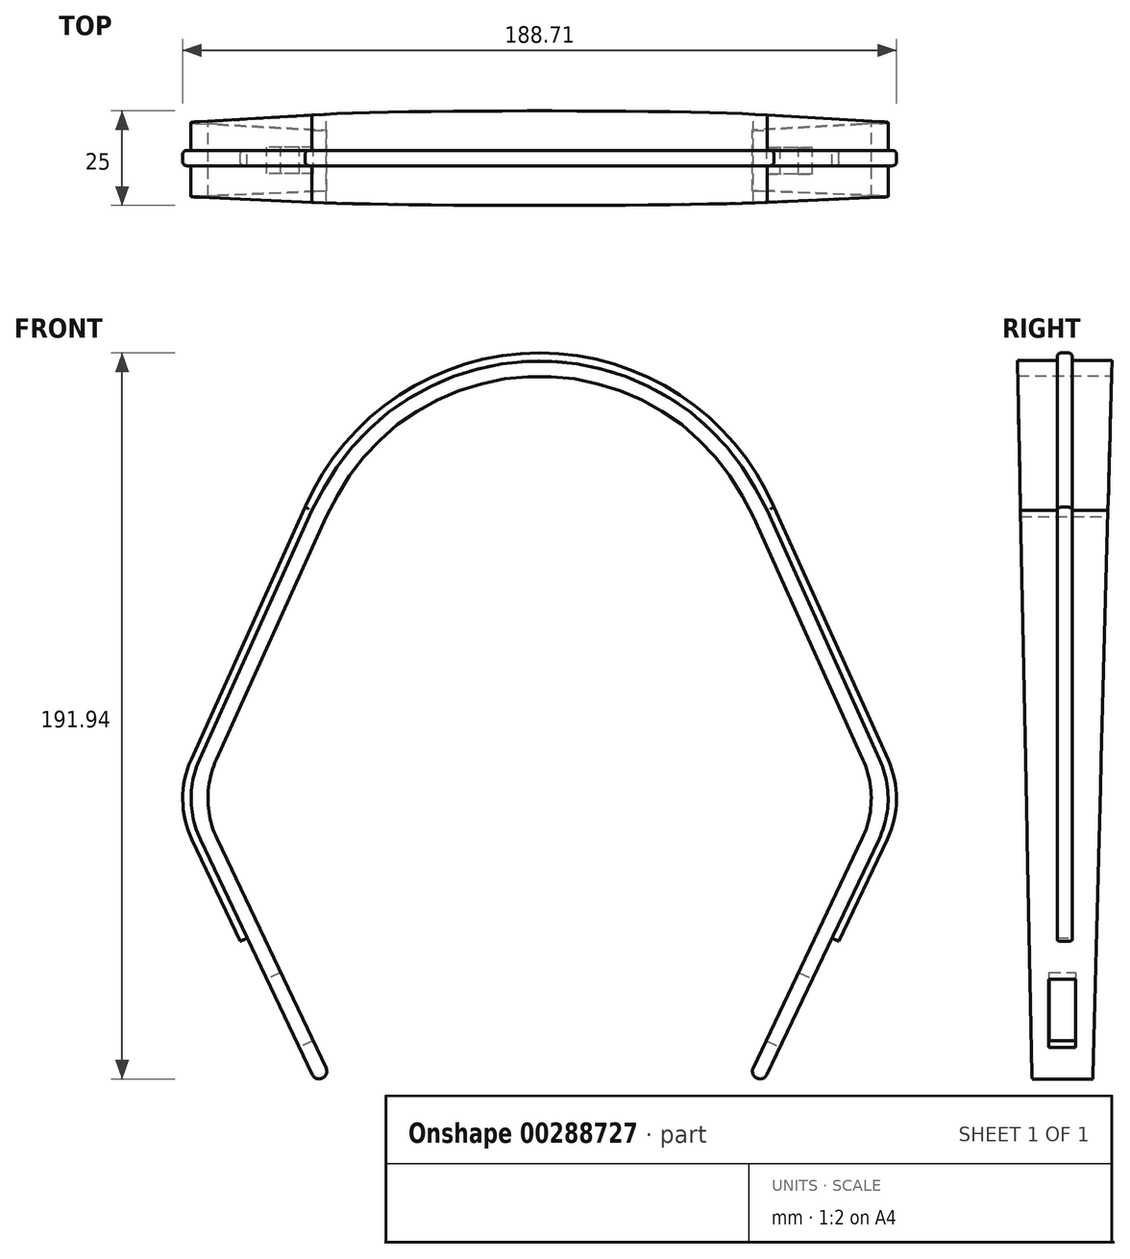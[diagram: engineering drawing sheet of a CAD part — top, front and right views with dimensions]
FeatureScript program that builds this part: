
annotation { "Feature Type Name" : "Feature", "Feature Type Description" : "" }
export const myFeature = defineFeature(function(context is Context, id is Id, definition is map)
    precondition{}
    {
        {
            var Q0;
            Q0=qCreatedBy(makeId("Right.planeOp"),FACE);
            cPlane(context, id + "F0", {"entities" : qUnion([Q0]), "cplaneType" : CPlaneType.OFFSET, "offset" : 144.2 * mm, "oppositeDirection" : true, "width" : 150 * mm, "height" : 150 * mm});
        }
        {
            var Q0;
            Q0=qCreatedBy(makeId("Front.planeOp"),FACE);
            var sketch = newSketch(context, id + "F1", { "sketchPlane" : qUnion([Q0])});
            skLineSegment(sketch, "E0", {"start": v(94.64, 16.15) * mm, "end": v(60.84, -54.85) * mm});
            skPoint(sketch, "E1.orphan", {"position": v(-52.06, -54.85) * mm});
            skLineSegment(sketch, "E2", {"start": v(94.64, 16.15) * mm, "end": v(60.84, 90.95) * mm});
            skLineSegment(sketch, "E3.MirrorCS", {"start": v(-85.86, 16.15) * mm, "end": v(-52.06, -54.85) * mm});
            skLineSegment(sketch, "E4.MirrorCS", {"start": v(-85.86, 16.15) * mm, "end": v(-52.06, 90.95) * mm});
            skArc(sketch, "E5", {"start": v(60.84, 90.95) * mm, "mid": v(4.39, 128.15) * mm, "end": v(-52.06, 90.95) * mm});
            skLineSegment(sketch, "E6.0", {"start": v(-90.32, 16.1) * mm, "end": v(-55.71, -56.59) * mm});
            skLineSegment(sketch, "E6.1", {"start": v(99.1, 16.1) * mm, "end": v(64.49, -56.59) * mm});
            skLineSegment(sketch, "E6.2", {"start": v(99.1, 16.1) * mm, "end": v(64.54, 92.58) * mm});
            skArc(sketch, "E6.3", {"start": v(64.54, 92.58) * mm, "mid": v(4.39, 132.2) * mm, "end": v(-55.76, 92.58) * mm});
            skLineSegment(sketch, "E6.4", {"start": v(-90.32, 16.1) * mm, "end": v(-55.76, 92.58) * mm});
            skArc(sketch, "E7", {"start": v(-55.71, -56.59) * mm, "mid": v(-53.02, -57.54) * mm, "end": v(-52.06, -54.85) * mm});
            skArc(sketch, "E8", {"start": v(60.84, -54.85) * mm, "mid": v(61.8, -57.54) * mm, "end": v(64.49, -56.59) * mm});
            skSolve(sketch);
        }
        {
            var Q0;
            Q0 = qSketchRegion(id + "F1", true);
            extrude(context, id + "F2", {"entities" : qUnion([Q0]), "depth" : 10.5 * mm});
        }
        {
            var Q0;
            Q0=makeQuery(id+"F2.opExtrude","CAP_FACE",FACE,{"disambiguationData":[OSD([sQuery(id+"F1.wireOp",EDGE,"E0"),sQuery(id+"F1.wireOp",EDGE,"E2"),sQuery(id+"F1.wireOp",EDGE,"E3.MirrorCS"),sQuery(id+"F1.wireOp",EDGE,"E4.MirrorCS"),sQuery(id+"F1.wireOp",EDGE,"E5"),sQuery(id+"F1.wireOp",EDGE,"E6.0"),sQuery(id+"F1.wireOp",EDGE,"E6.1"),sQuery(id+"F1.wireOp",EDGE,"E6.2"),sQuery(id+"F1.wireOp",EDGE,"E6.3"),sQuery(id+"F1.wireOp",EDGE,"E6.4"),sQuery(id+"F1.wireOp",EDGE,"E7"),sQuery(id+"F1.wireOp",EDGE,"E8")])],"isStart":false});
            var sketch = newSketch(context, id + "F3", { "sketchPlane" : qUnion([Q0])});
            skLineSegment(sketch, "E9.0.0", {"start": v(-72.9, -20.47) * mm, "end": v(-55.71, -56.59) * mm});
            skArc(sketch, "E9.0.1", {"start": v(-55.71, -56.59) * mm, "mid": v(-53.02, -57.54) * mm, "end": v(-52.06, -54.85) * mm});
            skLineSegment(sketch, "E9.0.2", {"start": v(-52.06, -54.85) * mm, "end": v(-85.86, 16.15) * mm});
            skLineSegment(sketch, "E9.0.3", {"start": v(-85.86, 16.15) * mm, "end": v(-52.06, 90.95) * mm});
            skArc(sketch, "E9.0.4", {"start": v(-52.06, 90.95) * mm, "mid": v(4.39, 128.15) * mm, "end": v(60.84, 90.95) * mm});
            skLineSegment(sketch, "E9.0.5", {"start": v(60.84, 90.95) * mm, "end": v(94.64, 16.15) * mm});
            skLineSegment(sketch, "E9.0.6", {"start": v(94.64, 16.15) * mm, "end": v(60.84, -54.85) * mm});
            skArc(sketch, "E9.0.7", {"start": v(60.84, -54.85) * mm, "mid": v(61.8, -57.54) * mm, "end": v(64.49, -56.59) * mm});
            skLineSegment(sketch, "E9.0.8", {"start": v(64.49, -56.59) * mm, "end": v(81.68, -20.47) * mm});
            skLineSegment(sketch, "E10", {"start": v(-72.9, -20.47) * mm, "end": v(-74.71, -21.33) * mm});
            skLineSegment(sketch, "E11", {"start": v(-74.71, -21.33) * mm, "end": v(-92.53, 16.09) * mm});
            skLineSegment(sketch, "E12.0", {"start": v(-57.59, 93.4) * mm, "end": v(-92.14, 16.93) * mm});
            skLineSegment(sketch, "E13", {"start": v(-92.14, 16.93) * mm, "end": v(-92.53, 16.09) * mm});
            skPoint(sketch, "E9.0.11.end.orphan", {"position": v(-90.32, 16.1) * mm});
            skLineSegment(sketch, "E14.MirrorCS", {"start": v(66.36, 93.4) * mm, "end": v(100.92, 16.93) * mm});
            skLineSegment(sketch, "E15.MirrorCS", {"start": v(83.49, -21.33) * mm, "end": v(101.3, 16.09) * mm});
            skLineSegment(sketch, "E16.MirrorCS", {"start": v(100.92, 16.93) * mm, "end": v(101.3, 16.09) * mm});
            skArc(sketch, "E17", {"start": v(66.36, 93.4) * mm, "mid": v(4.39, 134.2) * mm, "end": v(-57.59, 93.4) * mm});
            skLineSegment(sketch, "E18", {"start": v(83.49, -21.33) * mm, "end": v(81.68, -20.47) * mm});
            skPoint(sketch, "E19.orphan", {"position": v(99.1, 16.1) * mm});
            skSolve(sketch);
        }
        {
            var Q0;
            Q0 = qSketchRegion(id + "F3", true);
            extrude(context, id + "F4", {"entities" : qUnion([Q0]), "operationType" : NewBodyOperationType.ADD, "depth" : 4 * mm});
        }
        {
            var Q0;
            Q0=makeQuery(id+"F4.opExtrude","CAP_FACE",FACE,{"disambiguationData":[OSD([sQuery(id+"F3.wireOp",EDGE,"E9.0.0"),sQuery(id+"F3.wireOp",EDGE,"E9.0.1"),sQuery(id+"F3.wireOp",EDGE,"E9.0.2"),sQuery(id+"F3.wireOp",EDGE,"E9.0.3"),sQuery(id+"F3.wireOp",EDGE,"E9.0.4"),sQuery(id+"F3.wireOp",EDGE,"E9.0.5"),sQuery(id+"F3.wireOp",EDGE,"E9.0.6"),sQuery(id+"F3.wireOp",EDGE,"E9.0.7"),sQuery(id+"F3.wireOp",EDGE,"E9.0.8"),sQuery(id+"F3.wireOp",EDGE,"E10"),sQuery(id+"F3.wireOp",EDGE,"E11"),sQuery(id+"F3.wireOp",EDGE,"E12.0"),sQuery(id+"F3.wireOp",EDGE,"E13"),sQuery(id+"F3.wireOp",EDGE,"E14.MirrorCS"),sQuery(id+"F3.wireOp",EDGE,"E15.MirrorCS"),sQuery(id+"F3.wireOp",EDGE,"E16.MirrorCS"),sQuery(id+"F3.wireOp",EDGE,"E17"),sQuery(id+"F3.wireOp",EDGE,"E18")])],"isStart":false});
            var sketch = newSketch(context, id + "F5", { "sketchPlane" : qUnion([Q0])});
            skLineSegment(sketch, "E20.0.0", {"start": v(-55.71, -56.59) * mm, "end": v(-90.32, 16.1) * mm});
            skLineSegment(sketch, "E20.0.1", {"start": v(-90.32, 16.1) * mm, "end": v(-55.76, 92.58) * mm});
            skArc(sketch, "E20.0.2", {"start": v(-55.76, 92.58) * mm, "mid": v(4.39, 132.2) * mm, "end": v(64.54, 92.58) * mm});
            skLineSegment(sketch, "E20.0.3", {"start": v(64.54, 92.58) * mm, "end": v(99.1, 16.1) * mm});
            skLineSegment(sketch, "E20.0.4", {"start": v(99.1, 16.1) * mm, "end": v(64.49, -56.59) * mm});
            skArc(sketch, "E20.0.5", {"start": v(64.49, -56.59) * mm, "mid": v(61.8, -57.54) * mm, "end": v(60.84, -54.85) * mm});
            skLineSegment(sketch, "E20.0.6", {"start": v(60.84, -54.85) * mm, "end": v(94.64, 16.15) * mm});
            skLineSegment(sketch, "E20.0.7", {"start": v(94.64, 16.15) * mm, "end": v(60.84, 90.95) * mm});
            skArc(sketch, "E20.0.8", {"start": v(60.84, 90.95) * mm, "mid": v(4.39, 128.15) * mm, "end": v(-52.06, 90.95) * mm});
            skLineSegment(sketch, "E20.0.9", {"start": v(-52.06, 90.95) * mm, "end": v(-85.86, 16.15) * mm});
            skLineSegment(sketch, "E20.0.10", {"start": v(-85.86, 16.15) * mm, "end": v(-52.06, -54.85) * mm});
            skArc(sketch, "E20.0.11", {"start": v(-52.06, -54.85) * mm, "mid": v(-53.02, -57.54) * mm, "end": v(-55.71, -56.59) * mm});
            skSolve(sketch);
        }
        {
            var Q0;
            Q0 = qSketchRegion(id + "F5", true);
            extrude(context, id + "F6", {"entities" : qUnion([Q0]), "operationType" : NewBodyOperationType.ADD, "depth" : 10.5 * mm});
        }
        {
            var Q0;
            Q0=qCreatedBy(id+"F0.planeOp",FACE);
            var sketch = newSketch(context, id + "F7", { "sketchPlane" : qUnion([Q0])});
            skLineSegment(sketch, "E21.0", {"start": v(0, 16.1) * mm, "end": v(0, 92.58) * mm});
            skLineSegment(sketch, "E22.0", {"start": v(-25, 16.1) * mm, "end": v(-25, 92.58) * mm});
            skLineSegment(sketch, "E23.0", {"start": v(-25, -56.59) * mm, "end": v(-25, 16.1) * mm});
            skLineSegment(sketch, "E24.0", {"start": v(0, 16.1) * mm, "end": v(0, -56.59) * mm});
            skLineSegment(sketch, "E25.0", {"start": v(-25, -57.74) * mm, "end": v(-25, -54.85) * mm});
            skLineSegment(sketch, "E26", {"start": v(0, -57.74) * mm, "end": v(-5.12, -57.74) * mm});
            skLineSegment(sketch, "E27.0", {"start": v(0, -57.74) * mm, "end": v(0, -54.85) * mm});
            skPoint(sketch, "E28.orphan", {"position": v(-26.23, -57.74) * mm});
            skPoint(sketch, "E29.0.end.orphan", {"position": v(0, 132.2) * mm});
            skPoint(sketch, "E30.0.end.orphan", {"position": v(-25, 132.2) * mm});
            skPoint(sketch, "E31.start.orphan", {"position": v(-13.12, -57.74) * mm});
            skLineSegment(sketch, "E32.trimOffspring", {"start": v(-21.12, -57.74) * mm, "end": v(-25, -57.74) * mm});
            skLineSegment(sketch, "E33.0", {"start": v(-25, 92.58) * mm, "end": v(-25, 132.2) * mm});
            skLineSegment(sketch, "E34.0", {"start": v(0, 92.58) * mm, "end": v(0, 132.2) * mm});
            skLineSegment(sketch, "E35", {"start": v(-21.12, -57.74) * mm, "end": v(-25, 132.2) * mm});
            skLineSegment(sketch, "E36", {"start": v(-5.12, -57.74) * mm, "end": v(0, 132.2) * mm});
            skSolve(sketch);
        }
        {
            var Q0;
            Q0 = qSketchRegion(id + "F7", true);
            extrude(context, id + "F8", {"entities" : qUnion([Q0]), "operationType" : NewBodyOperationType.REMOVE, "depth" : 274.5 * mm});
        }
        {
            var Q0;
            Q0=makeQuery(id+"F6.boolean.opBoolean","MERGE",FACE,{"derivedFrom":[makeQuery(id+"F4.boolean.opBoolean","MERGE",FACE,{"derivedFrom":[makeQuery(id+"F2.opExtrude","SWEPT_FACE",FACE,{"disambiguationData":[OSD([sQuery(id+"F1.wireOp",EDGE,"E6.0")])]}),makeQuery(id+"F4.opExtrude","SWEPT_FACE",FACE,{"disambiguationData":[OSD([sQuery(id+"F3.wireOp",EDGE,"E9.0.0")])]})]}),makeQuery(id+"F6.opExtrude","SWEPT_FACE",FACE,{"disambiguationData":[OSD([sQuery(id+"F5.wireOp",EDGE,"E20.0.0")])]})]});
            cPlane(context, id + "F9", {"entities" : qUnion([Q0]), "cplaneType" : CPlaneType.OFFSET, "offset" : 25 * mm, "width" : 150 * mm, "height" : 150 * mm});
        }
        {
            var Q0;
            Q0=qCreatedBy(id+"F9.planeOp",FACE);
            var sketch = newSketch(context, id + "F10", { "sketchPlane" : qUnion([Q0])});
            skLineSegment(sketch, "E37", {"start": v(13.12, 0.83) * mm, "end": v(16.62, 0.83) * mm});
            skLineSegment(sketch, "E38", {"start": v(16.62, 0.83) * mm, "end": v(16.62, -19.17) * mm});
            skLineSegment(sketch, "E39.MirrorCS", {"start": v(13.12, 0.83) * mm, "end": v(9.62, 0.83) * mm});
            skLineSegment(sketch, "E40.MirrorCS", {"start": v(9.62, 0.83) * mm, "end": v(9.62, -19.17) * mm});
            skLineSegment(sketch, "E41", {"start": v(9.62, -19.17) * mm, "end": v(16.62, -19.17) * mm});
            skSolve(sketch);
        }
        {
            var Q0;
            Q0 = qSketchRegion(id + "F10", true);
            extrude(context, id + "F11", {"entities" : qUnion([Q0]), "operationType" : NewBodyOperationType.REMOVE, "oppositeDirection" : true, "depth" : 42.7 * mm});
        }
        {
            var Q0;
            Q0=makeQuery(id+"F6.opExtrude","SWEPT_EDGE",EDGE,{"disambiguationData":[OSD([sQuery(id+"F5.wireOp",EDGE,"E20.0.0"),sQuery(id+"F5.wireOp",EDGE,"E20.0.1")])]});
            var Q1;
            Q1=makeQuery(id+"F4.opExtrude","SWEPT_EDGE",EDGE,{"disambiguationData":[OSD([sQuery(id+"F3.wireOp",EDGE,"E11"),sQuery(id+"F3.wireOp",EDGE,"E13")])]});
            var Q2;
            Q2=makeQuery(id+"F2.opExtrude","SWEPT_EDGE",EDGE,{"disambiguationData":[OSD([sQuery(id+"F1.wireOp",EDGE,"E6.0"),sQuery(id+"F1.wireOp",EDGE,"E6.4")])]});
            var Q3;
            Q3=makeQuery(id+"F6.boolean.opBoolean","MERGE",EDGE,{"derivedFrom":[makeQuery(id+"F4.boolean.opBoolean","MERGE",EDGE,{"derivedFrom":[makeQuery(id+"F2.opExtrude","SWEPT_EDGE",EDGE,{"disambiguationData":[OSD([sQuery(id+"F1.wireOp",EDGE,"E3.MirrorCS"),sQuery(id+"F1.wireOp",EDGE,"E4.MirrorCS")])]}),makeQuery(id+"F4.opExtrude","SWEPT_EDGE",EDGE,{"disambiguationData":[OSD([sQuery(id+"F3.wireOp",EDGE,"E9.0.2"),sQuery(id+"F3.wireOp",EDGE,"E9.0.3")])]})]}),makeQuery(id+"F6.opExtrude","SWEPT_EDGE",EDGE,{"disambiguationData":[OSD([sQuery(id+"F5.wireOp",EDGE,"E20.0.9"),sQuery(id+"F5.wireOp",EDGE,"E20.0.10")])]})]});
            fillet(context, id + "F12", {"entities" : qUnion([Q0, Q1, Q2, Q3]), "radius" : 25 * mm, "tangentPropagation" : true, "allowEdgeOverflow" : false});
        }
        {
            var Q0;
            Q0=makeQuery(id+"F6.boolean.opBoolean","MERGE",FACE,{"derivedFrom":[makeQuery(id+"F4.boolean.opBoolean","MERGE",FACE,{"derivedFrom":[makeQuery(id+"F2.opExtrude","SWEPT_FACE",FACE,{"disambiguationData":[OSD([sQuery(id+"F1.wireOp",EDGE,"E6.1")])]}),makeQuery(id+"F4.opExtrude","SWEPT_FACE",FACE,{"disambiguationData":[OSD([sQuery(id+"F3.wireOp",EDGE,"E9.0.8")])]})]}),makeQuery(id+"F6.opExtrude","SWEPT_FACE",FACE,{"disambiguationData":[OSD([sQuery(id+"F5.wireOp",EDGE,"E20.0.4")])]})]});
            cPlane(context, id + "F13", {"entities" : qUnion([Q0]), "cplaneType" : CPlaneType.OFFSET, "offset" : 25 * mm, "width" : 150 * mm, "height" : 150 * mm});
        }
        {
            var Q0;
            Q0=qCreatedBy(id+"F13.planeOp",FACE);
            var sketch = newSketch(context, id + "F14", { "sketchPlane" : qUnion([Q0])});
            skLineSegment(sketch, "E42", {"start": v(-13.19, 4.6) * mm, "end": v(-16.69, 4.6) * mm});
            skLineSegment(sketch, "E43", {"start": v(-16.69, 4.6) * mm, "end": v(-16.69, -15.4) * mm});
            skLineSegment(sketch, "E44", {"start": v(-13.19, -15.4) * mm, "end": v(-16.69, -15.4) * mm});
            skLineSegment(sketch, "E45.MirrorCS", {"start": v(-13.19, -15.4) * mm, "end": v(-9.69, -15.4) * mm});
            skLineSegment(sketch, "E46.MirrorCS", {"start": v(-9.69, 4.6) * mm, "end": v(-9.69, -15.4) * mm});
            skLineSegment(sketch, "E47.MirrorCS", {"start": v(-13.19, 4.6) * mm, "end": v(-9.69, 4.6) * mm});
            skSolve(sketch);
        }
        {
            var Q0;
            Q0 = qSketchRegion(id + "F14", true);
            extrude(context, id + "F15", {"entities" : qUnion([Q0]), "operationType" : NewBodyOperationType.REMOVE, "oppositeDirection" : true, "depth" : 50.6 * mm});
        }
        {
            var Q0;
            Q0=makeQuery(id+"F6.opExtrude","SWEPT_EDGE",EDGE,{"disambiguationData":[OSD([sQuery(id+"F5.wireOp",EDGE,"E20.0.3"),sQuery(id+"F5.wireOp",EDGE,"E20.0.4")])]});
            var Q1;
            Q1=makeQuery(id+"F2.opExtrude","SWEPT_EDGE",EDGE,{"disambiguationData":[OSD([sQuery(id+"F1.wireOp",EDGE,"E6.1"),sQuery(id+"F1.wireOp",EDGE,"E6.2")])]});
            var Q2;
            Q2=makeQuery(id+"F4.opExtrude","SWEPT_EDGE",EDGE,{"disambiguationData":[OSD([sQuery(id+"F3.wireOp",EDGE,"E15.MirrorCS"),sQuery(id+"F3.wireOp",EDGE,"E16.MirrorCS")])]});
            var Q3;
            Q3=makeQuery(id+"F6.boolean.opBoolean","MERGE",EDGE,{"derivedFrom":[makeQuery(id+"F4.boolean.opBoolean","MERGE",EDGE,{"derivedFrom":[makeQuery(id+"F2.opExtrude","SWEPT_EDGE",EDGE,{"disambiguationData":[OSD([sQuery(id+"F1.wireOp",EDGE,"E0"),sQuery(id+"F1.wireOp",EDGE,"E2")])]}),makeQuery(id+"F4.opExtrude","SWEPT_EDGE",EDGE,{"disambiguationData":[OSD([sQuery(id+"F3.wireOp",EDGE,"E9.0.5"),sQuery(id+"F3.wireOp",EDGE,"E9.0.6")])]})]}),makeQuery(id+"F6.opExtrude","SWEPT_EDGE",EDGE,{"disambiguationData":[OSD([sQuery(id+"F5.wireOp",EDGE,"E20.0.6"),sQuery(id+"F5.wireOp",EDGE,"E20.0.7")])]})]});
            fillet(context, id + "F16", {"entities" : qUnion([Q0, Q1, Q2, Q3]), "radius" : 25 * mm, "tangentPropagation" : true, "allowEdgeOverflow" : false});
        }
        {
            var Q0;
            Q0=makeQuery(id+"F4.opExtrude","CAP_EDGE",EDGE,{"disambiguationData":[OSD([sQuery(id+"F3.wireOp",EDGE,"E15.MirrorCS")])],"isStart":false});
            var Q1;
            Q1=makeQuery(id+"F4.opExtrude","CAP_EDGE",EDGE,{"disambiguationData":[OSD([sQuery(id+"F3.wireOp",EDGE,"E15.MirrorCS")])],"isStart":true});
            var Q2;
            {var subQ0=sQuery(id+"F3.wireOp",EDGE,"E16.MirrorCS");var subQ1=sQuery(id+"F3.wireOp",EDGE,"E15.MirrorCS");Q2=makeQuery(id+"F16.opFillet","BLEND_EDGE",EDGE,{"blendedFrom":[makeQuery(id+"F4.opExtrude","SWEPT_EDGE",EDGE,{"disambiguationData":[OSD([subQ1,subQ0])]}),makeQuery(id+"F4.opExtrude","CAP_FACE",FACE,{"disambiguationData":[OSD([sQuery(id+"F3.wireOp",EDGE,"E9.0.0"),sQuery(id+"F3.wireOp",EDGE,"E9.0.1"),sQuery(id+"F3.wireOp",EDGE,"E9.0.2"),sQuery(id+"F3.wireOp",EDGE,"E9.0.3"),sQuery(id+"F3.wireOp",EDGE,"E9.0.4"),sQuery(id+"F3.wireOp",EDGE,"E9.0.5"),sQuery(id+"F3.wireOp",EDGE,"E9.0.6"),sQuery(id+"F3.wireOp",EDGE,"E9.0.7"),sQuery(id+"F3.wireOp",EDGE,"E9.0.8"),sQuery(id+"F3.wireOp",EDGE,"E10"),sQuery(id+"F3.wireOp",EDGE,"E11"),sQuery(id+"F3.wireOp",EDGE,"E12.0"),sQuery(id+"F3.wireOp",EDGE,"E13"),sQuery(id+"F3.wireOp",EDGE,"E14.MirrorCS"),subQ1,subQ0,sQuery(id+"F3.wireOp",EDGE,"E17"),sQuery(id+"F3.wireOp",EDGE,"E18")])],"isStart":false})],"blendedInto":[makeQuery(id+"F4.opExtrude","CAP_FACE",FACE,{"disambiguationData":[OSD([sQuery(id+"F3.wireOp",EDGE,"E9.0.0"),sQuery(id+"F3.wireOp",EDGE,"E9.0.1"),sQuery(id+"F3.wireOp",EDGE,"E9.0.2"),sQuery(id+"F3.wireOp",EDGE,"E9.0.3"),sQuery(id+"F3.wireOp",EDGE,"E9.0.4"),sQuery(id+"F3.wireOp",EDGE,"E9.0.5"),sQuery(id+"F3.wireOp",EDGE,"E9.0.6"),sQuery(id+"F3.wireOp",EDGE,"E9.0.7"),sQuery(id+"F3.wireOp",EDGE,"E9.0.8"),sQuery(id+"F3.wireOp",EDGE,"E10"),sQuery(id+"F3.wireOp",EDGE,"E11"),sQuery(id+"F3.wireOp",EDGE,"E12.0"),sQuery(id+"F3.wireOp",EDGE,"E13"),sQuery(id+"F3.wireOp",EDGE,"E14.MirrorCS"),subQ1,subQ0,sQuery(id+"F3.wireOp",EDGE,"E17"),sQuery(id+"F3.wireOp",EDGE,"E18")])],"isStart":false})]});}
            var Q3;
            {var subQ0=sQuery(id+"F3.wireOp",EDGE,"E16.MirrorCS");var subQ1=sQuery(id+"F3.wireOp",EDGE,"E15.MirrorCS");Q3=makeQuery(id+"F16.opFillet","BLEND_EDGE",EDGE,{"blendedFrom":[makeQuery(id+"F4.opExtrude","SWEPT_EDGE",EDGE,{"disambiguationData":[OSD([subQ1,subQ0])]}),makeQuery(id+"F4.opExtrude","CAP_FACE",FACE,{"disambiguationData":[OSD([sQuery(id+"F3.wireOp",EDGE,"E9.0.0"),sQuery(id+"F3.wireOp",EDGE,"E9.0.1"),sQuery(id+"F3.wireOp",EDGE,"E9.0.2"),sQuery(id+"F3.wireOp",EDGE,"E9.0.3"),sQuery(id+"F3.wireOp",EDGE,"E9.0.4"),sQuery(id+"F3.wireOp",EDGE,"E9.0.5"),sQuery(id+"F3.wireOp",EDGE,"E9.0.6"),sQuery(id+"F3.wireOp",EDGE,"E9.0.7"),sQuery(id+"F3.wireOp",EDGE,"E9.0.8"),sQuery(id+"F3.wireOp",EDGE,"E10"),sQuery(id+"F3.wireOp",EDGE,"E11"),sQuery(id+"F3.wireOp",EDGE,"E12.0"),sQuery(id+"F3.wireOp",EDGE,"E13"),sQuery(id+"F3.wireOp",EDGE,"E14.MirrorCS"),subQ1,subQ0,sQuery(id+"F3.wireOp",EDGE,"E17"),sQuery(id+"F3.wireOp",EDGE,"E18")])],"isStart":true})],"blendedInto":[makeQuery(id+"F4.opExtrude","CAP_FACE",FACE,{"disambiguationData":[OSD([sQuery(id+"F3.wireOp",EDGE,"E9.0.0"),sQuery(id+"F3.wireOp",EDGE,"E9.0.1"),sQuery(id+"F3.wireOp",EDGE,"E9.0.2"),sQuery(id+"F3.wireOp",EDGE,"E9.0.3"),sQuery(id+"F3.wireOp",EDGE,"E9.0.4"),sQuery(id+"F3.wireOp",EDGE,"E9.0.5"),sQuery(id+"F3.wireOp",EDGE,"E9.0.6"),sQuery(id+"F3.wireOp",EDGE,"E9.0.7"),sQuery(id+"F3.wireOp",EDGE,"E9.0.8"),sQuery(id+"F3.wireOp",EDGE,"E10"),sQuery(id+"F3.wireOp",EDGE,"E11"),sQuery(id+"F3.wireOp",EDGE,"E12.0"),sQuery(id+"F3.wireOp",EDGE,"E13"),sQuery(id+"F3.wireOp",EDGE,"E14.MirrorCS"),subQ1,subQ0,sQuery(id+"F3.wireOp",EDGE,"E17"),sQuery(id+"F3.wireOp",EDGE,"E18")])],"isStart":true})]});}
            var Q4;
            Q4=makeQuery(id+"F4.opExtrude","CAP_EDGE",EDGE,{"disambiguationData":[OSD([sQuery(id+"F3.wireOp",EDGE,"E14.MirrorCS"),sQuery(id+"F3.wireOp",EDGE,"E16.MirrorCS")])],"isStart":false});
            var Q5;
            Q5=makeQuery(id+"F4.opExtrude","CAP_EDGE",EDGE,{"disambiguationData":[OSD([sQuery(id+"F3.wireOp",EDGE,"E17")])],"isStart":false});
            var Q6;
            Q6=makeQuery(id+"F4.opExtrude","CAP_EDGE",EDGE,{"disambiguationData":[OSD([sQuery(id+"F3.wireOp",EDGE,"E17")])],"isStart":true});
            var Q7;
            Q7=makeQuery(id+"F4.opExtrude","CAP_EDGE",EDGE,{"disambiguationData":[OSD([sQuery(id+"F3.wireOp",EDGE,"E11")])],"isStart":false});
            var Q8;
            Q8=makeQuery(id+"F4.opExtrude","CAP_EDGE",EDGE,{"disambiguationData":[OSD([sQuery(id+"F3.wireOp",EDGE,"E11")])],"isStart":true});
            var Q9;
            {var subQ0=sQuery(id+"F3.wireOp",EDGE,"E13");var subQ1=sQuery(id+"F3.wireOp",EDGE,"E11");Q9=makeQuery(id+"F12.opFillet","BLEND_EDGE",EDGE,{"blendedFrom":[makeQuery(id+"F4.opExtrude","SWEPT_EDGE",EDGE,{"disambiguationData":[OSD([subQ1,subQ0])]}),makeQuery(id+"F4.opExtrude","CAP_FACE",FACE,{"disambiguationData":[OSD([sQuery(id+"F3.wireOp",EDGE,"E9.0.0"),sQuery(id+"F3.wireOp",EDGE,"E9.0.1"),sQuery(id+"F3.wireOp",EDGE,"E9.0.2"),sQuery(id+"F3.wireOp",EDGE,"E9.0.3"),sQuery(id+"F3.wireOp",EDGE,"E9.0.4"),sQuery(id+"F3.wireOp",EDGE,"E9.0.5"),sQuery(id+"F3.wireOp",EDGE,"E9.0.6"),sQuery(id+"F3.wireOp",EDGE,"E9.0.7"),sQuery(id+"F3.wireOp",EDGE,"E9.0.8"),sQuery(id+"F3.wireOp",EDGE,"E10"),subQ1,sQuery(id+"F3.wireOp",EDGE,"E12.0"),subQ0,sQuery(id+"F3.wireOp",EDGE,"E14.MirrorCS"),sQuery(id+"F3.wireOp",EDGE,"E15.MirrorCS"),sQuery(id+"F3.wireOp",EDGE,"E16.MirrorCS"),sQuery(id+"F3.wireOp",EDGE,"E17"),sQuery(id+"F3.wireOp",EDGE,"E18")])],"isStart":true})],"blendedInto":[makeQuery(id+"F4.opExtrude","CAP_FACE",FACE,{"disambiguationData":[OSD([sQuery(id+"F3.wireOp",EDGE,"E9.0.0"),sQuery(id+"F3.wireOp",EDGE,"E9.0.1"),sQuery(id+"F3.wireOp",EDGE,"E9.0.2"),sQuery(id+"F3.wireOp",EDGE,"E9.0.3"),sQuery(id+"F3.wireOp",EDGE,"E9.0.4"),sQuery(id+"F3.wireOp",EDGE,"E9.0.5"),sQuery(id+"F3.wireOp",EDGE,"E9.0.6"),sQuery(id+"F3.wireOp",EDGE,"E9.0.7"),sQuery(id+"F3.wireOp",EDGE,"E9.0.8"),sQuery(id+"F3.wireOp",EDGE,"E10"),subQ1,sQuery(id+"F3.wireOp",EDGE,"E12.0"),subQ0,sQuery(id+"F3.wireOp",EDGE,"E14.MirrorCS"),sQuery(id+"F3.wireOp",EDGE,"E15.MirrorCS"),sQuery(id+"F3.wireOp",EDGE,"E16.MirrorCS"),sQuery(id+"F3.wireOp",EDGE,"E17"),sQuery(id+"F3.wireOp",EDGE,"E18")])],"isStart":true})]});}
            var Q10;
            {var subQ0=sQuery(id+"F3.wireOp",EDGE,"E13");var subQ1=sQuery(id+"F3.wireOp",EDGE,"E11");Q10=makeQuery(id+"F12.opFillet","BLEND_EDGE",EDGE,{"blendedFrom":[makeQuery(id+"F4.opExtrude","SWEPT_EDGE",EDGE,{"disambiguationData":[OSD([subQ1,subQ0])]}),makeQuery(id+"F4.opExtrude","CAP_FACE",FACE,{"disambiguationData":[OSD([sQuery(id+"F3.wireOp",EDGE,"E9.0.0"),sQuery(id+"F3.wireOp",EDGE,"E9.0.1"),sQuery(id+"F3.wireOp",EDGE,"E9.0.2"),sQuery(id+"F3.wireOp",EDGE,"E9.0.3"),sQuery(id+"F3.wireOp",EDGE,"E9.0.4"),sQuery(id+"F3.wireOp",EDGE,"E9.0.5"),sQuery(id+"F3.wireOp",EDGE,"E9.0.6"),sQuery(id+"F3.wireOp",EDGE,"E9.0.7"),sQuery(id+"F3.wireOp",EDGE,"E9.0.8"),sQuery(id+"F3.wireOp",EDGE,"E10"),subQ1,sQuery(id+"F3.wireOp",EDGE,"E12.0"),subQ0,sQuery(id+"F3.wireOp",EDGE,"E14.MirrorCS"),sQuery(id+"F3.wireOp",EDGE,"E15.MirrorCS"),sQuery(id+"F3.wireOp",EDGE,"E16.MirrorCS"),sQuery(id+"F3.wireOp",EDGE,"E17"),sQuery(id+"F3.wireOp",EDGE,"E18")])],"isStart":false})],"blendedInto":[makeQuery(id+"F4.opExtrude","CAP_FACE",FACE,{"disambiguationData":[OSD([sQuery(id+"F3.wireOp",EDGE,"E9.0.0"),sQuery(id+"F3.wireOp",EDGE,"E9.0.1"),sQuery(id+"F3.wireOp",EDGE,"E9.0.2"),sQuery(id+"F3.wireOp",EDGE,"E9.0.3"),sQuery(id+"F3.wireOp",EDGE,"E9.0.4"),sQuery(id+"F3.wireOp",EDGE,"E9.0.5"),sQuery(id+"F3.wireOp",EDGE,"E9.0.6"),sQuery(id+"F3.wireOp",EDGE,"E9.0.7"),sQuery(id+"F3.wireOp",EDGE,"E9.0.8"),sQuery(id+"F3.wireOp",EDGE,"E10"),subQ1,sQuery(id+"F3.wireOp",EDGE,"E12.0"),subQ0,sQuery(id+"F3.wireOp",EDGE,"E14.MirrorCS"),sQuery(id+"F3.wireOp",EDGE,"E15.MirrorCS"),sQuery(id+"F3.wireOp",EDGE,"E16.MirrorCS"),sQuery(id+"F3.wireOp",EDGE,"E17"),sQuery(id+"F3.wireOp",EDGE,"E18")])],"isStart":false})]});}
            var Q11;
            Q11=makeQuery(id+"F4.opExtrude","CAP_EDGE",EDGE,{"disambiguationData":[OSD([sQuery(id+"F3.wireOp",EDGE,"E12.0"),sQuery(id+"F3.wireOp",EDGE,"E13")])],"isStart":false});
            var Q12;
            Q12=makeQuery(id+"F4.opExtrude","CAP_EDGE",EDGE,{"disambiguationData":[OSD([sQuery(id+"F3.wireOp",EDGE,"E12.0"),sQuery(id+"F3.wireOp",EDGE,"E13")])],"isStart":true});
            var Q13;
            Q13=makeQuery(id+"F4.opExtrude","CAP_EDGE",EDGE,{"disambiguationData":[OSD([sQuery(id+"F3.wireOp",EDGE,"E14.MirrorCS"),sQuery(id+"F3.wireOp",EDGE,"E16.MirrorCS")])],"isStart":true});
            fillet(context, id + "F17", {"entities" : qUnion([Q0, Q1, Q2, Q3, Q4, Q5, Q6, Q7, Q8, Q9, Q10, Q11, Q12, Q13]), "radius" : 1 * mm, "tangentPropagation" : true, "allowEdgeOverflow" : false});
        }
    });
